annotation { "Feature Type Name" : "Feature", "Feature Type Description" : "" }
export const myFeature = defineFeature(function(context is Context, id is Id, definition is map)
    precondition{}
    {
        {
            var Q0;
            Q0=qCreatedBy(makeId("Front.planeOp"),FACE);
            var sketch = newSketch(context, id + "F0", { "sketchPlane" : qUnion([Q0])});
            skLineSegment(sketch, "E0.left", {"start": v(-13.11, 42.27) * mm, "end": v(-13.11, -59.33) * mm});
            skLineSegment(sketch, "E0.right", {"start": v(12.29, 42.27) * mm, "end": v(12.29, -30.33) * mm});
            skPoint(sketch, "E1.oppositeSnap0", {"position": v(-0.41, 42.27) * mm});
            skLineSegment(sketch, "E1.bottom", {"start": v(-76.5, 67.67) * mm, "end": v(75.9, 67.67) * mm});
            skLineSegment(sketch, "E1.top", {"start": v(-47.62, 42.27) * mm, "end": v(-13.11, 42.27) * mm});
            skLineSegment(sketch, "E1.right", {"start": v(75.9, 67.67) * mm, "end": v(75.9, 65.45) * mm});
            skLineSegment(sketch, "E2", {"start": v(-76.5, 67.67) * mm, "end": v(-47.62, 42.27) * mm});
            skLineSegment(sketch, "E3", {"start": v(-47.62, 42.27) * mm, "end": v(-76.5, 67.67) * mm});
            skLineSegment(sketch, "E4", {"start": v(75.9, 65.45) * mm, "end": v(75.9, 67.67) * mm});
            skLineSegment(sketch, "E5", {"start": v(75.9, 67.67) * mm, "end": v(47.03, 42.27) * mm});
            skPoint(sketch, "E6.orphan", {"position": v(75.9, 42.27) * mm});
            skLineSegment(sketch, "E7", {"start": v(-13.11, -59.33) * mm, "end": v(12.29, -30.33) * mm});
            skLineSegment(sketch, "E8.trimOffspring", {"start": v(12.29, 42.27) * mm, "end": v(47.03, 42.27) * mm});
            skLineSegment(sketch, "E9.bottom", {"start": v(12.29, 12.97) * mm, "end": v(50.39, 12.97) * mm});
            skLineSegment(sketch, "E9.top", {"start": v(12.29, -12.43) * mm, "end": v(26.38, -12.43) * mm});
            skLineSegment(sketch, "E9.left", {"start": v(12.29, 12.97) * mm, "end": v(12.29, -12.43) * mm});
            skLineSegment(sketch, "E10", {"start": v(50.39, 12.97) * mm, "end": v(26.38, -12.43) * mm});
            skLineSegment(sketch, "E11.bottom", {"start": v(-13.11, 19.55) * mm, "end": v(-51.21, 19.55) * mm});
            skLineSegment(sketch, "E11.top", {"start": v(-13.11, 6.85) * mm, "end": v(-36.28, 6.85) * mm});
            skLineSegment(sketch, "E11.left", {"start": v(-13.11, 19.55) * mm, "end": v(-13.11, 6.85) * mm});
            skLineSegment(sketch, "E12", {"start": v(-51.21, 19.55) * mm, "end": v(-36.28, 6.85) * mm});
            skSolve(sketch);
        }
        {
            var Q0;
            Q0=qSketchRegion(id+"F0",true);
            extrude(context, id + "F1", {"entities" : qUnion([Q0]), "depth" : 25.4 * mm});
        }
        {
            var Q0;
            Q0=makeQuery(id+"F1.opExtrude","CAP_EDGE",EDGE,{"disambiguationData":[OSD([sQuery(id+"F0.wireOp",EDGE,"E3")])],"isStart":false});
            var Q1;
            Q1=makeQuery(id+"F1.opExtrude","CAP_EDGE",EDGE,{"disambiguationData":[OSD([sQuery(id+"F0.wireOp",EDGE,"E5")])],"isStart":false});
            var Q2;
            Q2=makeQuery(id+"F1.opExtrude","CAP_EDGE",EDGE,{"disambiguationData":[OSD([sQuery(id+"F0.wireOp",EDGE,"E10")])],"isStart":false});
            var Q3;
            Q3=makeQuery(id+"F1.opExtrude","CAP_EDGE",EDGE,{"disambiguationData":[OSD([sQuery(id+"F0.wireOp",EDGE,"E12")])],"isStart":false});
            var Q4;
            Q4=makeQuery(id+"F1.opExtrude","CAP_EDGE",EDGE,{"disambiguationData":[OSD([sQuery(id+"F0.wireOp",EDGE,"E7")])],"isStart":false});
            var Q5;
            Q5=makeQuery(id+"F1.opExtrude","CAP_EDGE",EDGE,{"disambiguationData":[OSD([sQuery(id+"F0.wireOp",EDGE,"E12")])],"isStart":true});
            var Q6;
            Q6=makeQuery(id+"F1.opExtrude","CAP_EDGE",EDGE,{"disambiguationData":[OSD([sQuery(id+"F0.wireOp",EDGE,"E3")])],"isStart":true});
            var Q7;
            Q7=makeQuery(id+"F1.opExtrude","CAP_EDGE",EDGE,{"disambiguationData":[OSD([sQuery(id+"F0.wireOp",EDGE,"E5")])],"isStart":true});
            var Q8;
            Q8=makeQuery(id+"F1.opExtrude","CAP_EDGE",EDGE,{"disambiguationData":[OSD([sQuery(id+"F0.wireOp",EDGE,"E10")])],"isStart":true});
            var Q9;
            Q9=makeQuery(id+"F1.opExtrude","CAP_EDGE",EDGE,{"disambiguationData":[OSD([sQuery(id+"F0.wireOp",EDGE,"E7")])],"isStart":true});
            fillet(context, id + "F2", {"entities" : qUnion([Q0, Q1, Q2, Q3, Q4, Q5, Q6, Q7, Q8, Q9]), "radius" : 5.08 * mm, "tangentPropagation" : true, "allowEdgeOverflow" : false});
        }
        {
            var Q0;
            Q0=makeQuery(id+"F1.opExtrude","CAP_FACE",FACE,{"disambiguationData":[OSD([sQuery(id+"F0.wireOp",EDGE,"E0.left"),sQuery(id+"F0.wireOp",EDGE,"E0.right"),sQuery(id+"F0.wireOp",EDGE,"E1.bottom"),sQuery(id+"F0.wireOp",EDGE,"E1.top"),sQuery(id+"F0.wireOp",EDGE,"E3"),sQuery(id+"F0.wireOp",EDGE,"E5"),sQuery(id+"F0.wireOp",EDGE,"E7"),sQuery(id+"F0.wireOp",EDGE,"E8.trimOffspring"),sQuery(id+"F0.wireOp",EDGE,"E9.bottom"),sQuery(id+"F0.wireOp",EDGE,"E9.top"),sQuery(id+"F0.wireOp",EDGE,"E10"),sQuery(id+"F0.wireOp",EDGE,"E11.bottom"),sQuery(id+"F0.wireOp",EDGE,"E11.top"),sQuery(id+"F0.wireOp",EDGE,"E12")])],"isStart":false});
            var sketch = newSketch(context, id + "F3", { "sketchPlane" : qUnion([Q0])});
            skLineSegment(sketch, "E13.bottom", {"start": v(-62.97, -76.38) * mm, "end": v(57.49, -76.38) * mm});
            skLineSegment(sketch, "E13.top", {"start": v(-62.97, -50.7) * mm, "end": v(57.49, -50.7) * mm});
            skLineSegment(sketch, "E13.left", {"start": v(-62.97, -76.38) * mm, "end": v(-62.97, -50.7) * mm});
            skLineSegment(sketch, "E13.right", {"start": v(57.49, -76.38) * mm, "end": v(57.49, -50.7) * mm});
            skSolve(sketch);
        }
        {
            var Q0;
            Q0=qSketchRegion(id+"F3",true);
            extrude(context, id + "F4", {"entities" : qUnion([Q0]), "operationType" : NewBodyOperationType.ADD, "oppositeDirection" : true, "depth" : 25.4 * mm});
        }
        {
            var Q0;
            Q0=makeQuery(id+"F4.boolean.opBoolean","MERGE",FACE,{"derivedFrom":[makeQuery(id+"F1.opExtrude","CAP_FACE",FACE,{"disambiguationData":[OSD([sQuery(id+"F0.wireOp",EDGE,"E0.left"),sQuery(id+"F0.wireOp",EDGE,"E0.right"),sQuery(id+"F0.wireOp",EDGE,"E1.bottom"),sQuery(id+"F0.wireOp",EDGE,"E1.top"),sQuery(id+"F0.wireOp",EDGE,"E3"),sQuery(id+"F0.wireOp",EDGE,"E5"),sQuery(id+"F0.wireOp",EDGE,"E7"),sQuery(id+"F0.wireOp",EDGE,"E8.trimOffspring"),sQuery(id+"F0.wireOp",EDGE,"E9.bottom"),sQuery(id+"F0.wireOp",EDGE,"E9.top"),sQuery(id+"F0.wireOp",EDGE,"E10"),sQuery(id+"F0.wireOp",EDGE,"E11.bottom"),sQuery(id+"F0.wireOp",EDGE,"E11.top"),sQuery(id+"F0.wireOp",EDGE,"E12")])],"isStart":false}),makeQuery(id+"F4.opExtrude","CAP_FACE",FACE,{"disambiguationData":[OSD([sQuery(id+"F3.wireOp",EDGE,"E13.bottom"),sQuery(id+"F3.wireOp",EDGE,"E13.top"),sQuery(id+"F3.wireOp",EDGE,"E13.left"),sQuery(id+"F3.wireOp",EDGE,"E13.right")])],"isStart":true})]});
            var sketch = newSketch(context, id + "F5", { "sketchPlane" : qUnion([Q0])});
            skText(sketch, "E14", { "text": "Faze Clan\n", "fontName": "OpenSans-Bold.ttf"});
            const initialGuessF5  = {"E14": [-0.0626, -0.07638, 1, 0, 0.01845]};
            skSetInitialGuess(sketch, initialGuessF5);
            skSolve(sketch);
        }
        {
            var Q0;
            Q0=qSketchRegion(id+"F5",true);
            extrude(context, id + "F6", {"entities" : qUnion([Q0]), "operationType" : NewBodyOperationType.ADD, "depth" : 2.54 * mm});
        }
    });